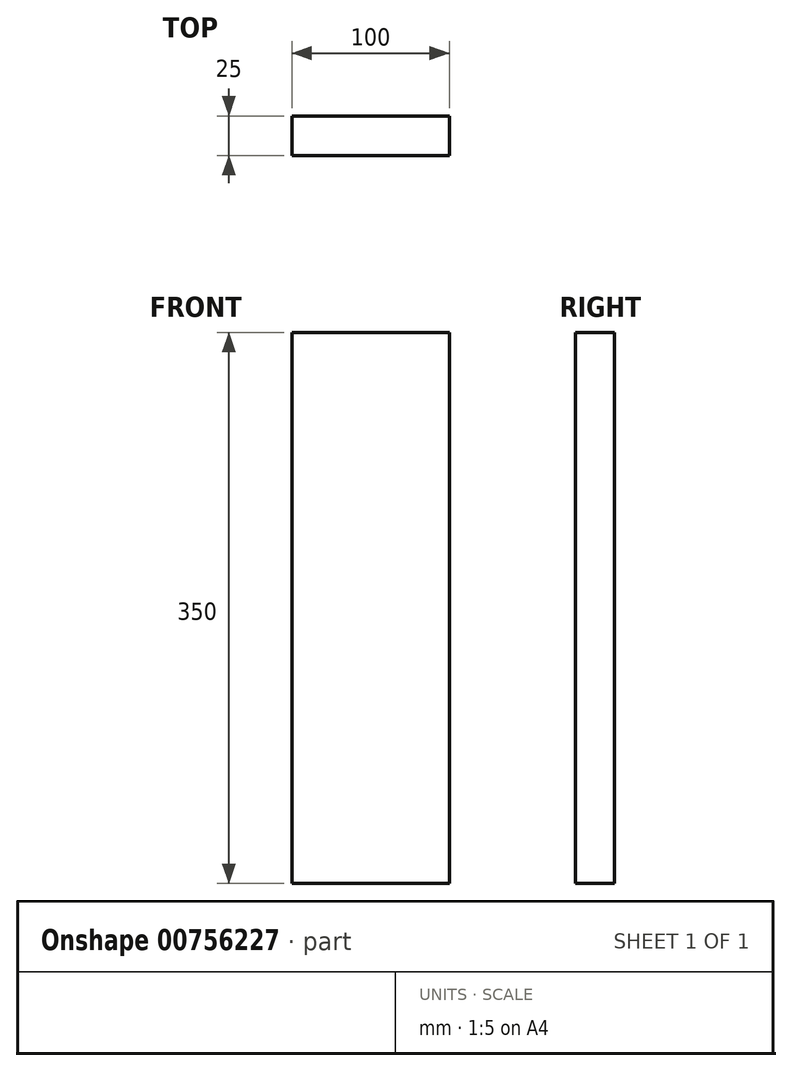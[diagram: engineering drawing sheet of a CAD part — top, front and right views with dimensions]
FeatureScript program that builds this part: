
annotation { "Feature Type Name" : "Feature", "Feature Type Description" : "" }
export const myFeature = defineFeature(function(context is Context, id is Id, definition is map)
    precondition{}
    {
        {
            var Q0;
            Q0=qCreatedBy(makeId("Front.planeOp"),FACE);
            var sketch = newSketch(context, id + "F0", { "sketchPlane" : qUnion([Q0])});
            skLineSegment(sketch, "E0.bottom", {"start": v(-47.91, 261.9) * mm, "end": v(52.09, 261.9) * mm});
            skLineSegment(sketch, "E0.top", {"start": v(-47.91, -88.1) * mm, "end": v(52.09, -88.1) * mm});
            skLineSegment(sketch, "E0.left", {"start": v(-47.91, 261.9) * mm, "end": v(-47.91, -88.1) * mm});
            skLineSegment(sketch, "E0.right", {"start": v(52.09, 261.9) * mm, "end": v(52.09, -88.1) * mm});
            skSolve(sketch);
        }
        {
            var Q0;
            Q0=makeQuery(id+"F0.imprint","IMPRINT",FACE,{"disambiguationData":[TD([[makeQuery(id+"F0.imprint","IMPRINT",EDGE,{"derivedFrom":sQuery(id+"F0.wireOp",EDGE,"E0.bottom")}),-1.0]])]});
            extrude(context, id + "F1", {"entities" : qUnion([Q0]), "depth" : 25 * mm, "offsetDistance" : 25 * mm});
        }
        {
            var Q0;
            Q0=makeQuery(id+"F0.imprint","IMPRINT",FACE,{"disambiguationData":[TD([[makeQuery(id+"F0.imprint","IMPRINT",EDGE,{"derivedFrom":sQuery(id+"F0.wireOp",EDGE,"E0.bottom")}),-1.0]])]});
            extrude(context, id + "F2", {"entities" : qUnion([Q0]), "operationType" : NewBodyOperationType.ADD, "depth" : 25 * mm, "offsetDistance" : 25 * mm});
        }
        {
            var Q0;
            Q0=makeQuery(id+"F0.imprint","IMPRINT",FACE,{"disambiguationData":[TD([[makeQuery(id+"F0.imprint","IMPRINT",EDGE,{"derivedFrom":sQuery(id+"F0.wireOp",EDGE,"E0.bottom")}),-1.0]])]});
            extrude(context, id + "F3", {"entities" : qUnion([Q0]), "operationType" : NewBodyOperationType.ADD, "depth" : 25 * mm, "offsetDistance" : 25 * mm});
        }
    });
